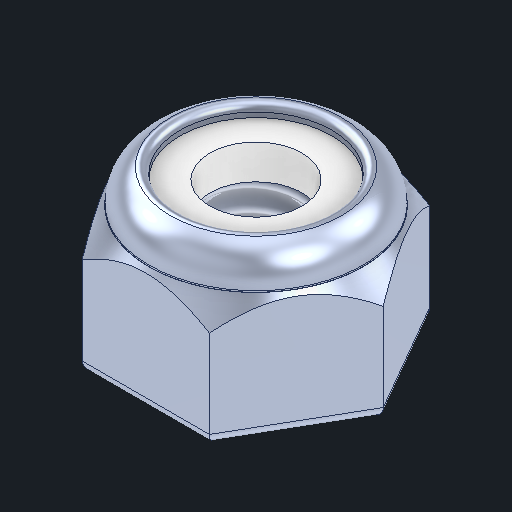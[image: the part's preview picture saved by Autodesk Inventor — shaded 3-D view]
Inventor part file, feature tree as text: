
AUTODESK INVENTOR PART (.ipt)
format: ipt  version: 2024 (Build 280153000, 153)  size: 224,768 bytes
history: native  units: in
note: dims shown in document units (in); Inventor stores cm internally (conversion verified against a paired STEP export)
features: other x4, plane x2, sketch x1
ambient origin geometry x8: Origin, YZ Plane, XZ Plane, XY Plane, X Axis, Y Axis, Z Axis, Center Point
bodies: Body1 (feature_tree)
feature tree (7):
  other  "Nut Nylock.ipt"
  other  "NONE::Nut Nylock.ipt"
  other  "TaggingFeature1"
  sketch  "Sketch1"  dims[d0=0.3937in]
  plane  "Work Plane1"
  plane  "Work Plane2"
  parser-record x1  (decoder bookkeeping rows leaked as tree rows — omitted from the tree; the rows remain in map.json)
